# Revit family: 01 - CASED EVOVERT - BTM IN - FRONT DIS - No Valves
name_source: partatom
category: Mechanical Equipment
revit_build: Autodesk Revit 2018 (Build: 20170223_1515(x64)
units: mm (PartAtom-declared; Revit-internal decimal feet)

## family parameters
Always vertical = Yes
Cut with Voids When Loaded = No
Host = Wall
OmniClass Number = 23.75.00.00
OmniClass Title = Climate Control (HVAC)
Part Type = Normal
Room Calculation Point = No
Round Connector Dimension = Use Diameter
Shared = No

## types (14) — shared parameters
AUX Pan Length = 125 mm
Access Clearance Bottom = 300 mm
Access Clearance Front = 150 mm  [stored 0.492126 ft]
Access Clearance Left = 150 mm  [stored 0.492126 ft]
Access Clearance Right = 150 mm  [stored 0.492126 ft]
Access Clearance Top = 300 mm
Access Panel Pos = 170 mm  [stored 0.557743 ft]
Air Flow Rate = 0.0 L/s
Assembly Code = D3050100
Back Panel Offset (Left) = 150 mm  [stored 0.492126 ft]
Back Panel Offset (Right) = 150 mm  [stored 0.492126 ft]
CHW Flow Temp. = 0
CHW Return Temp. = 0 °C
Ch.W Coil Connection Size = 15 mm  [stored 0.0492126 ft]
Ch.W Coil Flow = 0.0 L/s
Condensate Drain Connection Size = 15 mm  [stored 0.0492126 ft]
Condensate Drain Max Flow = 0.0 L/s
Condensate Tray = Yes
Configuration = Vertical
Control Valves & Actuators = No
Controls Connection = No
Cooling Coil Duty (Sensible) = 0 W
Cooling Coil Duty (Total) = 0 W
Description = Wall Mounted 235mm Deep and 510mm Tall Vertical Fan Coil Unit
Drain Connection Size = 15 mm  [stored 0.0492126 ft]
Drain Cut Size = 13 mm  [stored 0.0426509 ft]
Drain From Edge = 7.5 mm  [stored 0.0246063 ft]
Earth Connector = Yes
Electrical Enclosure Depth = 145 mm  [stored 0.475722 ft]
Electrical Enclosure Height = 380 mm  [stored 1.24672 ft]
Electrical Enclosure Width = 235 mm  [stored 0.770997 ft]
Electrical Power Consumption = 0 W
Electrical Supply Current (Max) = 0 A
Enclosure Depth (Model) = 143.8 mm
Enclosure Width (Model) = 233.8 mm
FCU Depth = 235 mm  [stored 0.770997 ft]
FCU Length = 510 mm  [stored 1.67323 ft]
Fan Type = Double Inlet Centrifugal
Heating Coil Duty Range = 0 W
Incoming Supply Electrical Frequency = 50 Hz
Incoming Supply Electrical Voltage = 230 V
Incoming Supply Phase = 1
Inlet Plenum = No
Intake Height = 180 mm
LPHW Flow Temperature = 0 °C
LPHW Return Temp. = 0 °C
LTHW Coil Connection Size = 15 mm  [stored 0.0492126 ft]
LTHW Coil Flow = 0.0 L/s
Low Voltage Transformer = No
Manufacturer = Ability Projects
Mat Thickness Neg = -1.2 mm  [stored -0.00393701 ft]
Mat Thickness Pos = 1.2 mm  [stored 0.00393701 ft]
Max Ext Press. = 0.0 Pa
Model = EVOVERT
Motor Enclosure Rating = IP42
Motor Type = EC
No of Outlet Connections = 1
Operating Weight = 0.00 kg
Outlet Connection Dia/Height = 100 mm  [stored 0.328084 ft]
Outlet Connection Shape = Rectangular
Overall Height = 235 mm  [stored 0.770997 ft]
Overall Length = 510 mm  [stored 1.67323 ft]
Pipe Connection Type = Screw
Primary Filter = G3
Return Air Temperature Sensor = No
Room Air Temperature Sensor = No
Shipping Weight = 0.00 kg
Speed Selection Controller = No
Starting Method = Soft Start
Summer Fresh Air Temp. = 0 °C
Summer On Coil Temp. = 0 °C
Summer Room Temp. = 0 °C
Summer off Coil Temp. = 0 °C
Temperature Controller = No
Winter Fresh Air Temp. = 0 °C
Winter On Coil Temp. = 0 °C
Winter Room Temp. = 0 °C
Winter off Coil Temp. = 0 °C
∆P Cooling Coil = 0.0 Pa
∆P Htg Coil = 0.0 Pa
zero-valued in all types: AUX Pan Extension, Inlet Connection Dia/Height, Inlet Connection Width, Sound Transmission (NR), Specific Fan Power

## per-type parameters (varying)
| type | FCU Width | Handing | Intake Width | LH Components Visible | Outlet Connection Width | Overall Width | RH Components Visible |
| EVOVERT - Size 100 LH | 670 mm  [stored 2.19816 ft] | LH | 640 mm  [stored 2.09974 ft] | Yes | 670 mm  [stored 2.19816 ft] | 970 mm  [stored 3.18241 ft] | No |
| EVOVERT - Size 100 RH | 670 mm  [stored 2.19816 ft] | RH | 640 mm  [stored 2.09974 ft] | No | 670 mm  [stored 2.19816 ft] | 970 mm  [stored 3.18241 ft] | Yes |
| EVOVERT - Size 200 LH | 970 mm  [stored 3.18241 ft] | LH | 940 mm | Yes | 970 mm  [stored 3.18241 ft] | 1270 mm | No |
| EVOVERT - Size 200 RH | 970 mm  [stored 3.18241 ft] | RH | 940 mm | No | 970 mm  [stored 3.18241 ft] | 1270 mm | Yes |
| EVOVERT - Size 250 LH | 970 mm  [stored 3.18241 ft] | LH | 940 mm | Yes | 970 mm  [stored 3.18241 ft] | 1270 mm | No |
| EVOVERT - Size 250 RH | 970 mm  [stored 3.18241 ft] | RH | 940 mm | No | 970 mm  [stored 3.18241 ft] | 1270 mm | Yes |
| EVOVERT - Size 300 LH | 1270 mm | LH | 1240 mm | Yes | 1270 mm | 1570 mm | No |
| EVOVERT - Size 300 RH | 1270 mm | RH | 1240 mm | No | 1270 mm | 1570 mm | Yes |
| EVOVERT - Size 400 LH | 1570 mm | LH | 1540 mm | Yes | 1570 mm | 1870 mm | No |
| EVOVERT - Size 400 RH | 1570 mm | RH | 1540 mm | No | 1570 mm | 1870 mm | Yes |
| EVOVERT - Size 500 LH | 1870 mm | LH | 1840 mm | Yes | 1870 mm | 2170 mm  [stored 7.11942 ft] | No |
| EVOVERT - Size 500 RH | 1870 mm | RH | 1840 mm | No | 1870 mm | 2170 mm  [stored 7.11942 ft] | Yes |
| EVOVERT - Size 550 LH | 1870 mm | LH | 1840 mm | Yes | 1870 mm | 2170 mm  [stored 7.11942 ft] | No |
| EVOVERT - Size 550 RH | 1870 mm | RH | 1840 mm | No | 1870 mm | 2170 mm  [stored 7.11942 ft] | Yes |

note: source unit labels omitted for CHW Flow Temp. — the stored unit's dimension contradicts the parameter name (converter mislabeling)

note: [stored X ft] marks values corroborated as IEEE doubles in the binary element streams (Revit-internal decimal feet)

## geometry (parser evidence)
native form markers: Blend x4, Sweep x9
no freeform markers — native parametric forms only
